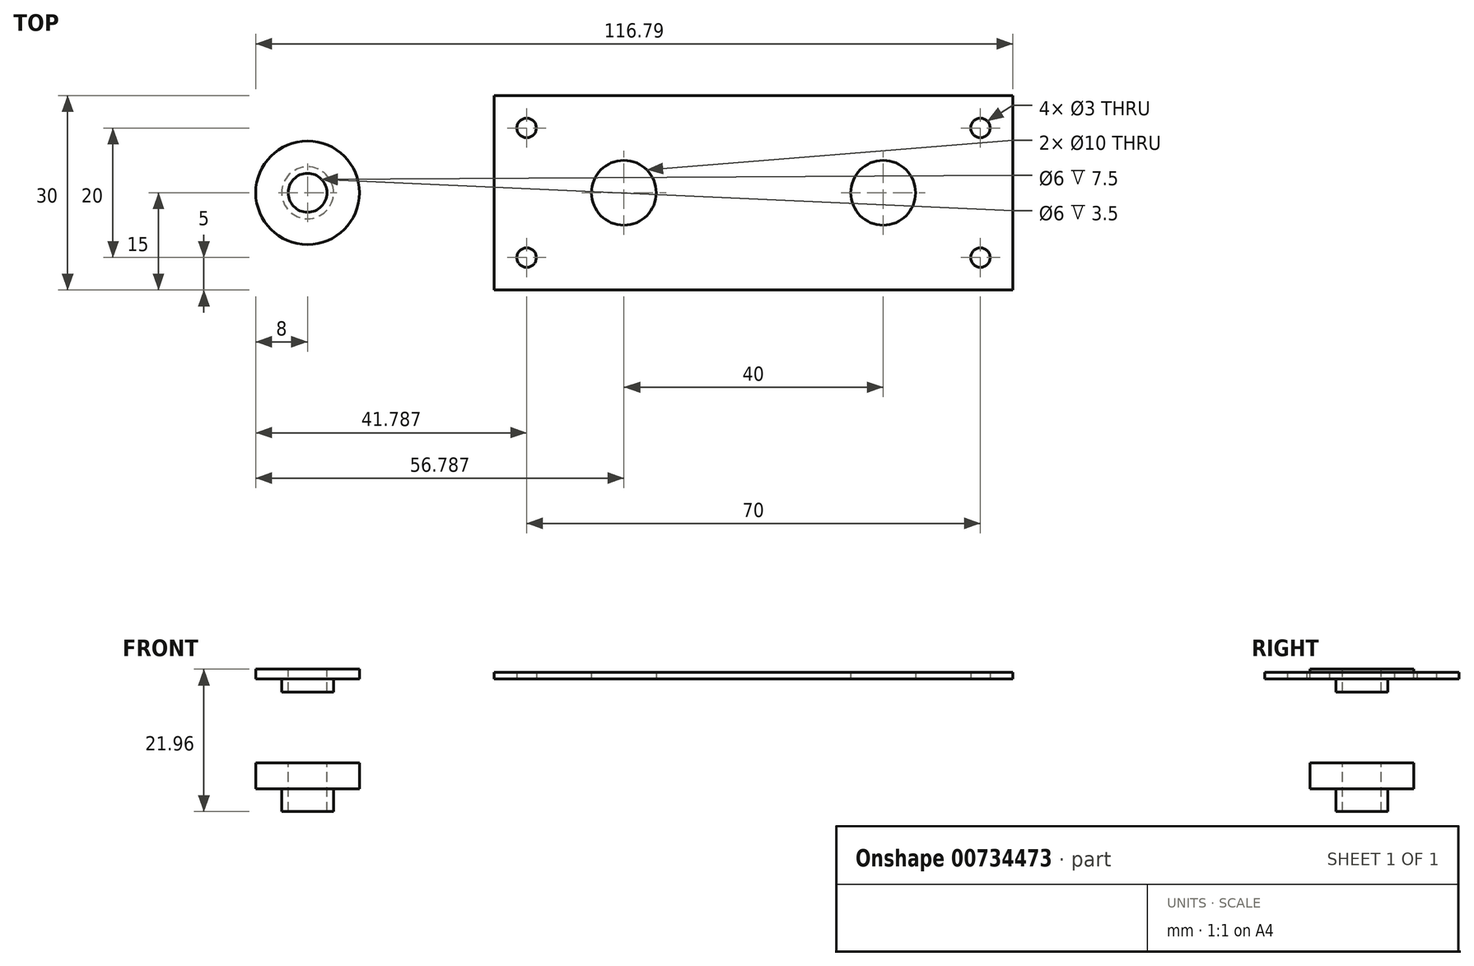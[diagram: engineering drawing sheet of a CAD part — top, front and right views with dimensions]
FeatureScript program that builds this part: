
annotation { "Feature Type Name" : "Feature", "Feature Type Description" : "" }
export const myFeature = defineFeature(function(context is Context, id is Id, definition is map)
    precondition{}
    {
        {
            var Q0;
            Q0=qCreatedBy(makeId("Front.planeOp"),FACE);
            var sketch = newSketch(context, id + "F0", { "sketchPlane" : qUnion([Q0])});
            skLineSegment(sketch, "E0", {"start": v(-3, 1.5) * mm, "end": v(-8, 1.5) * mm});
            skLineSegment(sketch, "E1", {"start": v(-8, 1.5) * mm, "end": v(-8, 0) * mm});
            skLineSegment(sketch, "E2", {"start": v(-8, 0) * mm, "end": v(-4, 0) * mm});
            skLineSegment(sketch, "E3", {"start": v(-4, 0) * mm, "end": v(-4, -2) * mm});
            skLineSegment(sketch, "E4", {"start": v(-4, -2) * mm, "end": v(-3, -2) * mm});
            skLineSegment(sketch, "E5", {"start": v(-3, -2) * mm, "end": v(-3, 1.5) * mm});
            skLineSegment(sketch, "E6", {"start": v(0, 13.9) * mm, "end": v(0, -9.75) * mm, "construction": true});
            skSolve(sketch);
        }
        {
            var Q0;
            Q0=qSketchRegion(id+"F0",true);
            var Q1;
            Q1=sQuery(id+"F0.wireOp",EDGE,"E6");
            revolve(context, id + "F1", {"surfaceOperationType" : NewSurfaceOperationType.NEW, "entities" : qUnion([Q0]), "axis" : qUnion([Q1]), "revolveType" : RevolveType.FULL});
        }
        {
            var Q0;
            Q0=qCreatedBy(makeId("Top.planeOp"),FACE);
            var sketch = newSketch(context, id + "F2", { "sketchPlane" : qUnion([Q0])});
            skLineSegment(sketch, "E7.bottom", {"start": v(28.79, 15) * mm, "end": v(108.79, 15) * mm});
            skLineSegment(sketch, "E7.top", {"start": v(28.79, -15) * mm, "end": v(108.79, -15) * mm});
            skLineSegment(sketch, "E7.left", {"start": v(28.79, 15) * mm, "end": v(28.79, -15) * mm});
            skLineSegment(sketch, "E7.right", {"start": v(108.79, 15) * mm, "end": v(108.79, -15) * mm});
            skLineSegment(sketch, "E8", {"start": v(68.79, 32.99) * mm, "end": v(68.79, -27.71) * mm, "construction": true});
            skLineSegment(sketch, "E9", {"start": v(25.97, 0) * mm, "end": v(115.92, 0) * mm, "construction": true});
            skPoint(sketch, "E9.endSnap0", {"position": v(108.79, 0) * mm});
            skCircle(sketch, "E10", {"center": v(33.79, 10) * mm, "radius": 1.5 * mm});
            skCircle(sketch, "E11.MirrorC", {"center": v(33.79, -10) * mm, "radius": 1.5 * mm});
            skLineSegment(sketch, "E12.MirrorCS", {"start": v(68.79, -32.99) * mm, "end": v(68.79, 27.71) * mm, "construction": true});
            skCircle(sketch, "E13.MirrorC", {"center": v(103.79, 10) * mm, "radius": 1.5 * mm});
            skCircle(sketch, "E14.MirrorC", {"center": v(103.79, -10) * mm, "radius": 1.5 * mm});
            skCircle(sketch, "E15", {"center": v(48.79, 0) * mm, "radius": 5 * mm});
            skCircle(sketch, "E16.MirrorC", {"center": v(88.79, 0) * mm, "radius": 5 * mm});
            skSolve(sketch);
        }
        {
            var Q0;
            Q0=qSketchRegion(id+"F2",true);
            extrude(context, id + "F3", {"entities" : qUnion([Q0]), "depth" : 1 * mm, "offsetDistance" : 25 * mm});
        }
        {
            var Q0;
            Q0=qCreatedBy(makeId("Front.planeOp"),FACE);
            var sketch = newSketch(context, id + "F4", { "sketchPlane" : qUnion([Q0])});
            skLineSegment(sketch, "E17", {"start": v(-3, -12.96) * mm, "end": v(-3, -20.46) * mm});
            skLineSegment(sketch, "E18", {"start": v(-3, -20.46) * mm, "end": v(-4, -20.46) * mm});
            skLineSegment(sketch, "E19", {"start": v(-4, -20.46) * mm, "end": v(-4, -16.96) * mm});
            skLineSegment(sketch, "E20", {"start": v(-4, -16.96) * mm, "end": v(-8, -16.96) * mm});
            skLineSegment(sketch, "E21", {"start": v(-8, -16.96) * mm, "end": v(-8, -12.96) * mm});
            skLineSegment(sketch, "E22", {"start": v(-8, -12.96) * mm, "end": v(-3, -12.96) * mm});
            skLineSegment(sketch, "E23", {"start": v(0, -6.52) * mm, "end": v(0, -28.57) * mm, "construction": true});
            skSolve(sketch);
        }
        {
            var Q0;
            Q0=qSketchRegion(id+"F4",true);
            var Q1;
            Q1=sQuery(id+"F4.wireOp",EDGE,"E23");
            revolve(context, id + "F5", {"surfaceOperationType" : NewSurfaceOperationType.NEW, "entities" : qUnion([Q0]), "axis" : qUnion([Q1]), "revolveType" : RevolveType.FULL});
        }
    });
